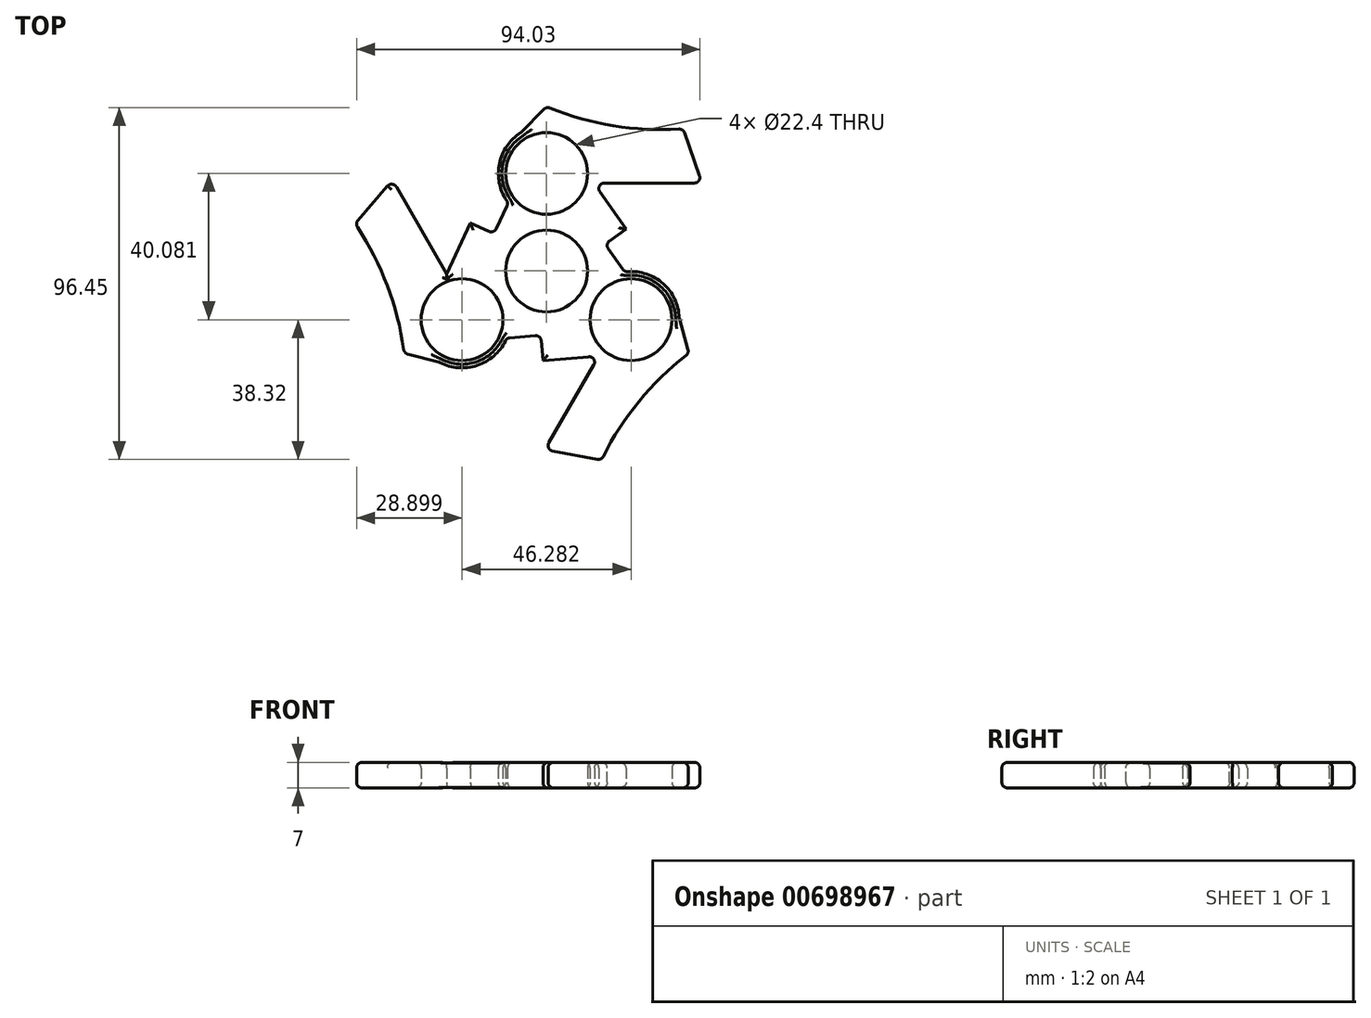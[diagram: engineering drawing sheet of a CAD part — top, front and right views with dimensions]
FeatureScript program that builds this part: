
annotation { "Feature Type Name" : "Feature", "Feature Type Description" : "" }
export const myFeature = defineFeature(function(context is Context, id is Id, definition is map)
    precondition{}
    {
        {
            var Q0;
            Q0=qCreatedBy(makeId("Top.planeOp"),FACE);
            var sketch = newSketch(context, id + "F0", { "sketchPlane" : qUnion([Q0])});
            skCircle(sketch, "E0", {"center": v(0, 0) * mm, "radius": 11.2 * mm});
            skCircle(sketch, "E1", {"center": v(0, 26.72) * mm, "radius": 11.2 * mm});
            skArc(sketch, "E2", {"start": v(-6.97, 37.93) * mm, "mid": v(-12.99, 29.07) * mm, "end": v(-10.46, 18.67) * mm});
            skCircle(sketch, "E3.1.0", {"center": v(-23.14, -13.36) * mm, "radius": 11.2 * mm});
            skArc(sketch, "E3.1.1", {"start": v(-29.36, -25) * mm, "mid": v(-18.68, -25.79) * mm, "end": v(-10.94, -18.4) * mm});
            skCircle(sketch, "E3.2.0", {"center": v(23.14, -13.36) * mm, "radius": 11.2 * mm});
            skArc(sketch, "E3.2.1", {"start": v(36.33, -12.93) * mm, "mid": v(31.67, -3.29) * mm, "end": v(21.4, -0.28) * mm});
            skLineSegment(sketch, "E4", {"start": v(12.94, 24.1) * mm, "end": v(42.6, 24.1) * mm});
            skLineSegment(sketch, "E5", {"start": v(42.6, 24.1) * mm, "end": v(37.4, 38.94) * mm});
            skArc(sketch, "E6", {"start": v(0, 45.04) * mm, "mid": v(18.35, 39.8) * mm, "end": v(37.4, 38.94) * mm});
            skLineSegment(sketch, "E7", {"start": v(12.94, 24.1) * mm, "end": v(21.83, 11.45) * mm});
            skLineSegment(sketch, "E8", {"start": v(21.83, 11.45) * mm, "end": v(16.02, 7.36) * mm});
            skLineSegment(sketch, "E9", {"start": v(16.02, 7.36) * mm, "end": v(21.4, -0.28) * mm});
            skArc(sketch, "E10.1.0", {"start": v(-39, -22.52) * mm, "mid": v(-43.64, -4) * mm, "end": v(-52.42, 12.93) * mm});
            skLineSegment(sketch, "E10.1.1", {"start": v(-27.34, -0.85) * mm, "end": v(-42.17, 24.84) * mm});
            skLineSegment(sketch, "E10.1.2", {"start": v(-42.17, 24.84) * mm, "end": v(-52.42, 12.93) * mm});
            skLineSegment(sketch, "E10.1.3", {"start": v(-27.34, -0.85) * mm, "end": v(-20.83, 13.18) * mm});
            skLineSegment(sketch, "E10.1.4", {"start": v(-20.83, 13.18) * mm, "end": v(-14.4, 10.2) * mm});
            skLineSegment(sketch, "E10.1.5", {"start": v(-14.4, 10.2) * mm, "end": v(-10.46, 18.67) * mm});
            skArc(sketch, "E10.2.0", {"start": v(39, -22.52) * mm, "mid": v(25.29, -35.79) * mm, "end": v(15.02, -51.87) * mm});
            skLineSegment(sketch, "E10.2.1", {"start": v(14.4, -23.25) * mm, "end": v(-0.43, -48.94) * mm});
            skLineSegment(sketch, "E10.2.2", {"start": v(-0.43, -48.94) * mm, "end": v(15.02, -51.87) * mm});
            skLineSegment(sketch, "E10.2.3", {"start": v(14.4, -23.25) * mm, "end": v(-1, -24.64) * mm});
            skLineSegment(sketch, "E10.2.4", {"start": v(-1, -24.64) * mm, "end": v(-1.63, -17.56) * mm});
            skLineSegment(sketch, "E10.2.5", {"start": v(-1.63, -17.56) * mm, "end": v(-10.94, -18.4) * mm});
            skLineSegment(sketch, "E11", {"start": v(0, 45.04) * mm, "end": v(-6.97, 37.93) * mm});
            skLineSegment(sketch, "E12.1.0", {"start": v(-39, -22.52) * mm, "end": v(-29.36, -25) * mm});
            skLineSegment(sketch, "E12.2.0", {"start": v(39, -22.52) * mm, "end": v(36.33, -12.93) * mm});
            skSolve(sketch);
        }
        {
            var Q0;
            Q0=makeQuery(id+"F0.imprint","IMPRINT",FACE,{"disambiguationData":[TD([[makeQuery(id+"F0.imprint","IMPRINT",EDGE,{"derivedFrom":sQuery(id+"F0.wireOp",EDGE,"E0")}),-1.0]])]});
            extrude(context, id + "F1", {"entities" : qUnion([Q0]), "depth" : 7 * mm, "offsetDistance" : 25 * mm});
        }
        {
            var Q0;
            Q0=makeQuery(id+"F1.opExtrude","CAP_FACE",FACE,{"disambiguationData":[OSD([sQuery(id+"F0.wireOp",EDGE,"E0"),sQuery(id+"F0.wireOp",EDGE,"E1"),sQuery(id+"F0.wireOp",EDGE,"E2"),sQuery(id+"F0.wireOp",EDGE,"E3.1.0"),sQuery(id+"F0.wireOp",EDGE,"E3.1.1"),sQuery(id+"F0.wireOp",EDGE,"E3.2.0"),sQuery(id+"F0.wireOp",EDGE,"E3.2.1"),sQuery(id+"F0.wireOp",EDGE,"E4"),sQuery(id+"F0.wireOp",EDGE,"E5"),sQuery(id+"F0.wireOp",EDGE,"E6"),sQuery(id+"F0.wireOp",EDGE,"E7"),sQuery(id+"F0.wireOp",EDGE,"E8"),sQuery(id+"F0.wireOp",EDGE,"E9"),sQuery(id+"F0.wireOp",EDGE,"E10.1.0"),sQuery(id+"F0.wireOp",EDGE,"E10.1.1"),sQuery(id+"F0.wireOp",EDGE,"E10.1.2"),sQuery(id+"F0.wireOp",EDGE,"E10.1.3"),sQuery(id+"F0.wireOp",EDGE,"E10.1.4"),sQuery(id+"F0.wireOp",EDGE,"E10.1.5"),sQuery(id+"F0.wireOp",EDGE,"E10.2.0"),sQuery(id+"F0.wireOp",EDGE,"E10.2.1"),sQuery(id+"F0.wireOp",EDGE,"E10.2.2"),sQuery(id+"F0.wireOp",EDGE,"E10.2.3"),sQuery(id+"F0.wireOp",EDGE,"E10.2.4"),sQuery(id+"F0.wireOp",EDGE,"E10.2.5"),sQuery(id+"F0.wireOp",EDGE,"E11"),sQuery(id+"F0.wireOp",EDGE,"E12.1.0"),sQuery(id+"F0.wireOp",EDGE,"E12.2.0")])],"isStart":false});
            var Q1;
            Q1=makeQuery(id+"F1.opExtrude","SWEPT_FACE",FACE,{"disambiguationData":[OSD([sQuery(id+"F0.wireOp",EDGE,"E10.1.0")])]});
            var Q2;
            Q2=makeQuery(id+"F1.opExtrude","SWEPT_EDGE",EDGE,{"disambiguationData":[OSD([sQuery(id+"F0.wireOp",EDGE,"E3.1.1"),sQuery(id+"F0.wireOp",EDGE,"E12.1.0")])]});
            var Q3;
            Q3=makeQuery(id+"F1.opExtrude","SWEPT_FACE",FACE,{"disambiguationData":[OSD([sQuery(id+"F0.wireOp",EDGE,"E10.1.2")])]});
            var Q4;
            Q4=makeQuery(id+"F1.opExtrude","SWEPT_FACE",FACE,{"disambiguationData":[OSD([sQuery(id+"F0.wireOp",EDGE,"E10.2.1")])]});
            var Q5;
            Q5=makeQuery(id+"F1.opExtrude","SWEPT_FACE",FACE,{"disambiguationData":[OSD([sQuery(id+"F0.wireOp",EDGE,"E6")])]});
            var Q6;
            Q6=makeQuery(id+"F1.opExtrude","SWEPT_FACE",FACE,{"disambiguationData":[OSD([sQuery(id+"F0.wireOp",EDGE,"E10.1.5")])]});
            var Q7;
            Q7=makeQuery(id+"F1.opExtrude","SWEPT_FACE",FACE,{"disambiguationData":[OSD([sQuery(id+"F0.wireOp",EDGE,"E10.1.5")])]});
            var Q8;
            Q8=makeQuery(id+"F1.opExtrude","SWEPT_FACE",FACE,{"disambiguationData":[OSD([sQuery(id+"F0.wireOp",EDGE,"E2")])]});
            var Q9;
            Q9=makeQuery(id+"F1.opExtrude","SWEPT_FACE",FACE,{"disambiguationData":[OSD([sQuery(id+"F0.wireOp",EDGE,"E11")])]});
            var Q10;
            Q10=makeQuery(id+"F1.opExtrude","SWEPT_FACE",FACE,{"disambiguationData":[OSD([sQuery(id+"F0.wireOp",EDGE,"E3.2.1")])]});
            var Q11;
            Q11=makeQuery(id+"F1.opExtrude","SWEPT_EDGE",EDGE,{"disambiguationData":[OSD([sQuery(id+"F0.wireOp",EDGE,"E8"),sQuery(id+"F0.wireOp",EDGE,"E9")])]});
            var Q12;
            Q12=makeQuery(id+"F1.opExtrude","CAP_EDGE",EDGE,{"disambiguationData":[OSD([sQuery(id+"F0.wireOp",EDGE,"E10.2.0")])],"isStart":false});
            var Q13;
            Q13=makeQuery(id+"F1.opExtrude","SWEPT_FACE",FACE,{"disambiguationData":[OSD([sQuery(id+"F0.wireOp",EDGE,"E10.2.0")])]});
            var Q14;
            Q14=makeQuery(id+"F1.opExtrude","CAP_EDGE",EDGE,{"disambiguationData":[OSD([sQuery(id+"F0.wireOp",EDGE,"E3.1.1")])],"isStart":false});
            var Q15;
            Q15=makeQuery(id+"F1.opExtrude","SWEPT_FACE",FACE,{"disambiguationData":[OSD([sQuery(id+"F0.wireOp",EDGE,"E12.1.0")])]});
            var Q16;
            Q16=makeQuery(id+"F1.opExtrude","SWEPT_FACE",FACE,{"disambiguationData":[OSD([sQuery(id+"F0.wireOp",EDGE,"E10.2.5")])]});
            var Q17;
            Q17=makeQuery(id+"F1.opExtrude","SWEPT_FACE",FACE,{"disambiguationData":[OSD([sQuery(id+"F0.wireOp",EDGE,"E10.2.2")])]});
            var Q18;
            Q18=makeQuery(id+"F1.opExtrude","SWEPT_EDGE",EDGE,{"disambiguationData":[OSD([sQuery(id+"F0.wireOp",EDGE,"E4"),sQuery(id+"F0.wireOp",EDGE,"E5")])]});
            var Q19;
            Q19=makeQuery(id+"F1.opExtrude","SWEPT_FACE",FACE,{"disambiguationData":[OSD([sQuery(id+"F0.wireOp",EDGE,"E4")])]});
            var Q20;
            Q20=makeQuery(id+"F1.opExtrude","CAP_FACE",FACE,{"disambiguationData":[OSD([sQuery(id+"F0.wireOp",EDGE,"E0"),sQuery(id+"F0.wireOp",EDGE,"E1"),sQuery(id+"F0.wireOp",EDGE,"E2"),sQuery(id+"F0.wireOp",EDGE,"E3.1.0"),sQuery(id+"F0.wireOp",EDGE,"E3.1.1"),sQuery(id+"F0.wireOp",EDGE,"E3.2.0"),sQuery(id+"F0.wireOp",EDGE,"E3.2.1"),sQuery(id+"F0.wireOp",EDGE,"E4"),sQuery(id+"F0.wireOp",EDGE,"E5"),sQuery(id+"F0.wireOp",EDGE,"E6"),sQuery(id+"F0.wireOp",EDGE,"E7"),sQuery(id+"F0.wireOp",EDGE,"E8"),sQuery(id+"F0.wireOp",EDGE,"E9"),sQuery(id+"F0.wireOp",EDGE,"E10.1.0"),sQuery(id+"F0.wireOp",EDGE,"E10.1.1"),sQuery(id+"F0.wireOp",EDGE,"E10.1.2"),sQuery(id+"F0.wireOp",EDGE,"E10.1.3"),sQuery(id+"F0.wireOp",EDGE,"E10.1.4"),sQuery(id+"F0.wireOp",EDGE,"E10.1.5"),sQuery(id+"F0.wireOp",EDGE,"E10.2.0"),sQuery(id+"F0.wireOp",EDGE,"E10.2.1"),sQuery(id+"F0.wireOp",EDGE,"E10.2.2"),sQuery(id+"F0.wireOp",EDGE,"E10.2.3"),sQuery(id+"F0.wireOp",EDGE,"E10.2.4"),sQuery(id+"F0.wireOp",EDGE,"E10.2.5"),sQuery(id+"F0.wireOp",EDGE,"E11"),sQuery(id+"F0.wireOp",EDGE,"E12.1.0"),sQuery(id+"F0.wireOp",EDGE,"E12.2.0")])],"isStart":true});
            fillet(context, id + "F2", {"entities" : qUnion([Q0, Q1, Q2, Q3, Q4, Q5, Q6, Q7, Q8, Q9, Q10, Q11, Q12, Q13, Q14, Q15, Q16, Q17, Q18, Q19, Q20]), "radius" : 1.5 * mm, "tangentPropagation" : true, "allowEdgeOverflow" : false});
        }
    });
